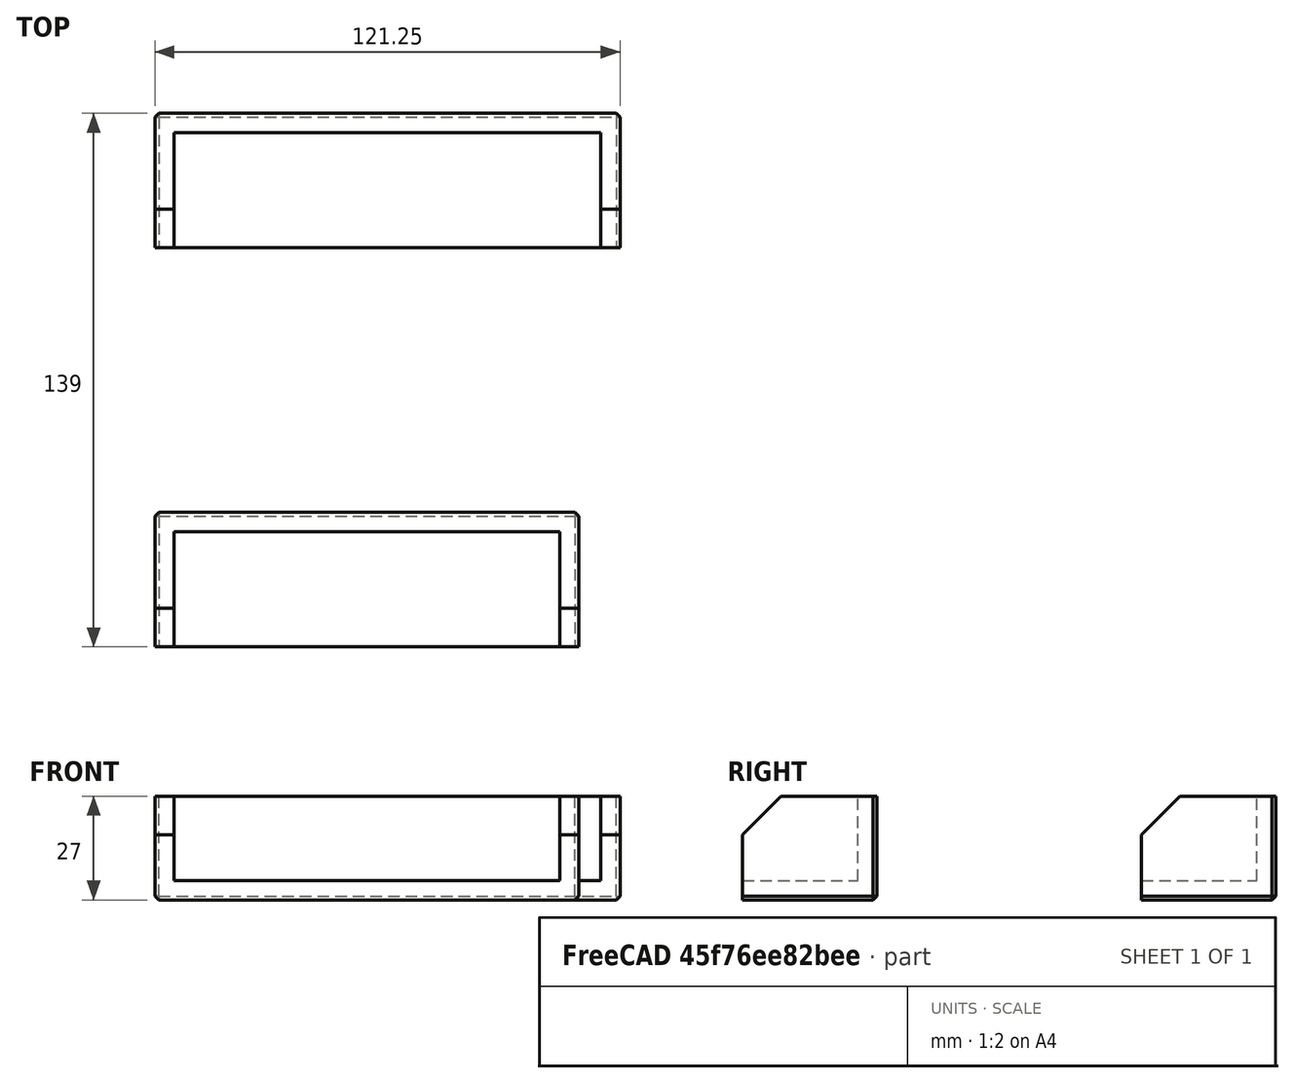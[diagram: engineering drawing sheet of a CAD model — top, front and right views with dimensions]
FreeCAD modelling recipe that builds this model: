
FCSTD DOCUMENT  (FreeCAD 0.19R23578 (Git))
Label: vise clamp
License: All rights reserved
LicenseURL: http://en.wikipedia.org/wiki/All_rights_reserved
objects: Part::Chamfer×4, Part::Box×2, Part::Thickness×2
note: 8 computed .brp shape members not serialized (recipe doc carries the construction recipe); baked Part::Feature solids carry a one-line shape summary decoded from their .brp

FEATURE [Part::Box] Box  label="Cube"
  AttacherType = Attacher::AttachEngine3D
  Height = 22
  Length = 111.25
  Width = 30
FEATURE [Part::Thickness] Thickness
  Faces = -> Box [Face3,Face6]
  Intersection = false
  Join = 2
  Mode = 0
  SelfIntersection = false
  Value = 5
FEATURE [Part::Chamfer] Chamfer
  Base = -> Thickness
  Edges = 2 edges r=10: [Edge12,Edge13]
FEATURE [Part::Chamfer] Chamfer001
  Base = -> Chamfer
  Edges = 5 edges r=1: [Edge26,Edge27,Edge28,Edge29,Edge30]
FEATURE [Part::Box] Box001  label="Cube001"
  AttacherType = Attacher::AttachEngine3D
  Height = 22
  Length = 100.5
  Width = 30
FEATURE [Part::Thickness] Thickness001
  Faces = -> Box001 [Face3,Face6]
  Intersection = false
  Join = 2
  Mode = 0
  SelfIntersection = false
  Value = 5
FEATURE [Part::Chamfer] Chamfer002
  Base = -> Thickness001
  Edges = 2 edges r=10: [Edge12,Edge13]
FEATURE [Part::Chamfer] Chamfer003
  Base = -> Chamfer002
  Edges = 5 edges r=1: [Edge26,Edge27,Edge28,Edge29,Edge30]
  Placement = pos=(0,-104,0) rot=(0,0,1;0rad)
